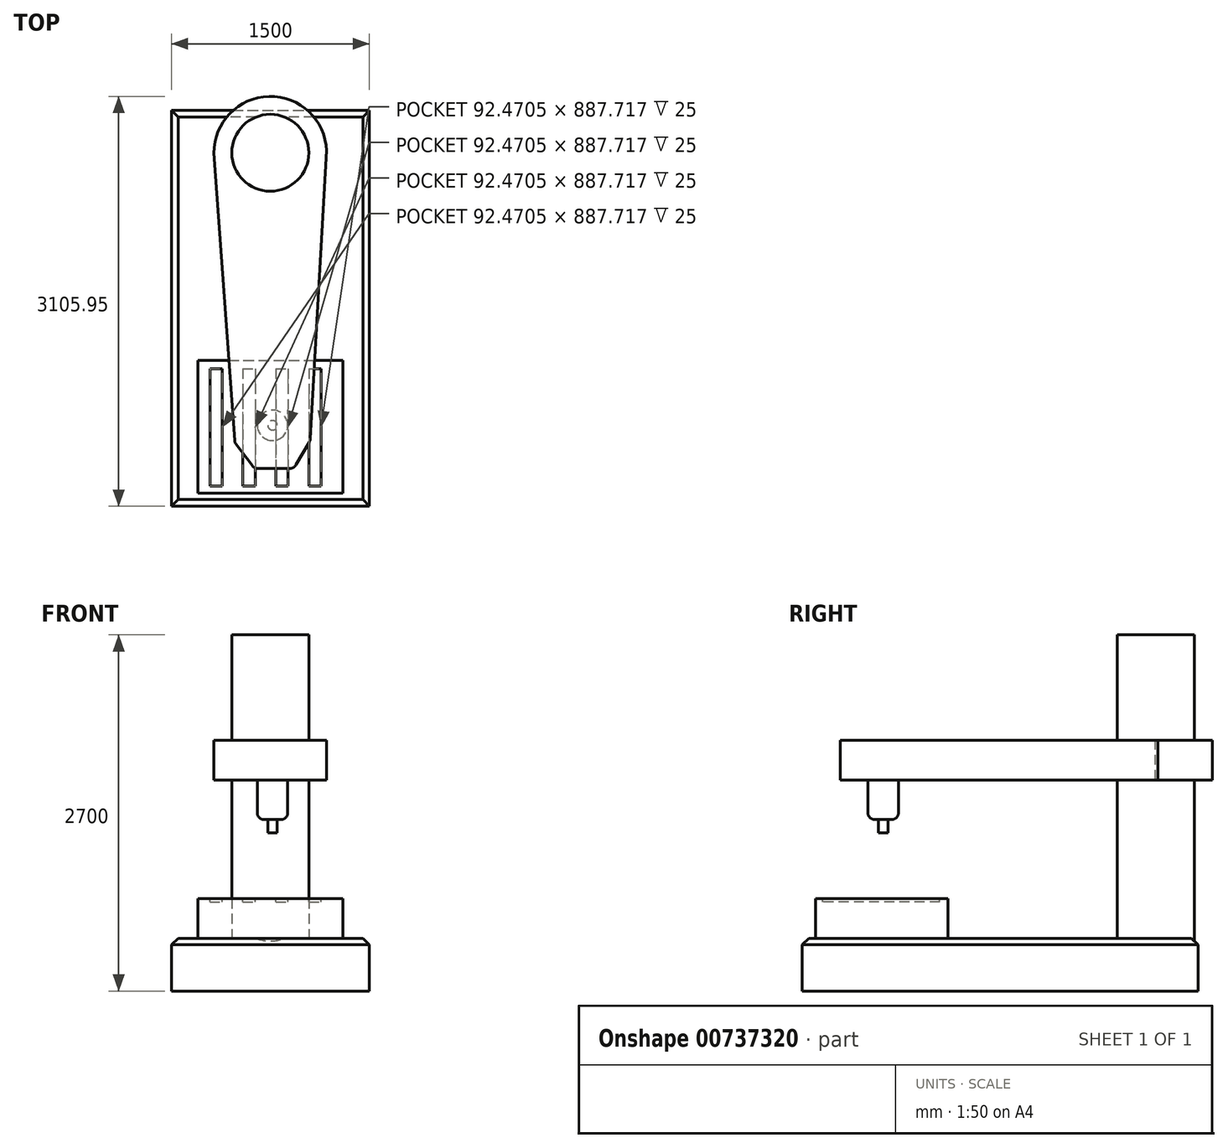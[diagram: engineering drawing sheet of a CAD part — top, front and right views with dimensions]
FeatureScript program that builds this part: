
annotation { "Feature Type Name" : "Feature", "Feature Type Description" : "" }
export const myFeature = defineFeature(function(context is Context, id is Id, definition is map)
    precondition{}
    {
        {
            var Q0;
            Q0=qCreatedBy(makeId("Top.planeOp"),FACE);
            var sketch = newSketch(context, id + "F0", { "sketchPlane" : qUnion([Q0])});
            skLineSegment(sketch, "E0.bottom", {"start": v(-749.39, 2386.8) * mm, "end": v(750.61, 2386.8) * mm});
            skLineSegment(sketch, "E0.top", {"start": v(-749.39, -613.2) * mm, "end": v(750.61, -613.2) * mm});
            skLineSegment(sketch, "E0.left", {"start": v(-749.39, 2386.8) * mm, "end": v(-749.39, -613.2) * mm});
            skLineSegment(sketch, "E0.right", {"start": v(750.61, 2386.8) * mm, "end": v(750.61, -613.2) * mm});
            skSolve(sketch);
        }
        {
            var Q0;
            Q0 = qSketchRegion(id + "F0", true);
            extrude(context, id + "F1", {"entities" : qUnion([Q0]), "depth" : 400 * mm, "offsetDistance" : 25 * mm});
        }
        {
            var Q0;
            Q0=makeQuery(id+"F1.opExtrude","CAP_FACE",FACE,{"disambiguationData":[OSD([sQuery(id+"F0.wireOp",EDGE,"E0.bottom"),sQuery(id+"F0.wireOp",EDGE,"E0.top"),sQuery(id+"F0.wireOp",EDGE,"E0.left"),sQuery(id+"F0.wireOp",EDGE,"E0.right")])],"isStart":false});
            var sketch = newSketch(context, id + "F2", { "sketchPlane" : qUnion([Q0])});
            skCircle(sketch, "E1", {"center": v(0, 2065.92) * mm, "radius": 292.28 * mm});
            skSolve(sketch);
        }
        {
            var Q0;
            Q0 = qSketchRegion(id + "F2", true);
            extrude(context, id + "F3", {"entities" : qUnion([Q0]), "operationType" : NewBodyOperationType.ADD, "depth" : 1500 * mm, "offsetDistance" : 25 * mm});
        }
        {
            var Q0;
            Q0=makeQuery(id+"F2.imprint","IMPRINT",FACE,{"disambiguationData":[TD([[makeQuery(id+"F2.imprint","IMPRINT",EDGE,{"derivedFrom":sQuery(id+"F2.wireOp",EDGE,"E1")}),-1.0]])]});
            var sketch = newSketch(context, id + "F4", { "sketchPlane" : qUnion([Q0])});
            skLineSegment(sketch, "E2.bottom", {"start": v(-549.39, 491.66) * mm, "end": v(550.61, 491.66) * mm});
            skLineSegment(sketch, "E2.top", {"start": v(-549.39, -513.2) * mm, "end": v(550.61, -513.2) * mm});
            skLineSegment(sketch, "E2.left", {"start": v(-549.39, 491.66) * mm, "end": v(-549.39, -513.2) * mm});
            skLineSegment(sketch, "E2.right", {"start": v(550.61, 491.66) * mm, "end": v(550.61, -513.2) * mm});
            skSolve(sketch);
        }
        {
            var Q0;
            Q0 = qSketchRegion(id + "F4", true);
            extrude(context, id + "F5", {"entities" : qUnion([Q0]), "depth" : 300 * mm, "offsetDistance" : 25 * mm});
        }
        {
            var Q0;
            Q0=makeQuery(id+"F5.opExtrude","CAP_FACE",FACE,{"disambiguationData":[OSD([sQuery(id+"F4.wireOp",EDGE,"E2.bottom"),sQuery(id+"F4.wireOp",EDGE,"E2.top"),sQuery(id+"F4.wireOp",EDGE,"E2.left"),sQuery(id+"F4.wireOp",EDGE,"E2.right")])],"isStart":false});
            var sketch = newSketch(context, id + "F6", { "sketchPlane" : qUnion([Q0])});
            skLineSegment(sketch, "E3.bottom", {"start": v(-457.37, 428.31) * mm, "end": v(-364.9, 428.31) * mm});
            skLineSegment(sketch, "E3.top", {"start": v(-457.37, -459.4) * mm, "end": v(-364.9, -459.4) * mm});
            skLineSegment(sketch, "E3.left", {"start": v(-457.37, 428.31) * mm, "end": v(-457.37, -459.4) * mm});
            skLineSegment(sketch, "E3.right", {"start": v(-364.9, 428.31) * mm, "end": v(-364.9, -459.4) * mm});
            skLineSegment(sketch, "E4.1.0.0", {"start": v(-207.37, 428.31) * mm, "end": v(-207.37, -459.4) * mm});
            skLineSegment(sketch, "E4.1.0.1", {"start": v(-114.9, 428.31) * mm, "end": v(-114.9, -459.4) * mm});
            skLineSegment(sketch, "E4.1.0.2", {"start": v(-207.37, -459.4) * mm, "end": v(-114.9, -459.4) * mm});
            skLineSegment(sketch, "E4.1.0.3", {"start": v(-207.37, 428.31) * mm, "end": v(-114.9, 428.31) * mm});
            skLineSegment(sketch, "E4.2.0.0", {"start": v(42.63, 428.31) * mm, "end": v(42.63, -459.4) * mm});
            skLineSegment(sketch, "E4.2.0.1", {"start": v(135.1, 428.31) * mm, "end": v(135.1, -459.4) * mm});
            skLineSegment(sketch, "E4.2.0.2", {"start": v(42.63, -459.4) * mm, "end": v(135.1, -459.4) * mm});
            skLineSegment(sketch, "E4.2.0.3", {"start": v(42.63, 428.31) * mm, "end": v(135.1, 428.31) * mm});
            skLineSegment(sketch, "E4.3.0.0", {"start": v(292.63, 428.31) * mm, "end": v(292.63, -459.4) * mm});
            skLineSegment(sketch, "E4.3.0.1", {"start": v(385.1, 428.31) * mm, "end": v(385.1, -459.4) * mm});
            skLineSegment(sketch, "E4.3.0.2", {"start": v(292.63, -459.4) * mm, "end": v(385.1, -459.4) * mm});
            skLineSegment(sketch, "E4.3.0.3", {"start": v(292.63, 428.31) * mm, "end": v(385.1, 428.31) * mm});
            skLineSegment(sketch, "E4.direction1", {"start": v(-457.37, -459.4) * mm, "end": v(-207.37, -459.4) * mm, "construction": true});
            skSolve(sketch);
        }
        {
            var Q0;
            Q0 = qSketchRegion(id + "F6", true);
            extrude(context, id + "F7", {"entities" : qUnion([Q0]), "operationType" : NewBodyOperationType.REMOVE, "oppositeDirection" : true, "depth" : 25 * mm, "offsetDistance" : 25 * mm});
        }
        {
            var Q0;
            Q0=makeQuery(id+"F3.opExtrude","CAP_FACE",FACE,{"disambiguationData":[OSD([sQuery(id+"F2.wireOp",EDGE,"E1")])],"isStart":false});
            var sketch = newSketch(context, id + "F8", { "sketchPlane" : qUnion([Q0])});
            skArc(sketch, "E5", {"start": v(-426.83, 2063.09) * mm, "mid": v(-9.46, 2492.65) * mm, "end": v(426.53, 2082.01) * mm});
            skLineSegment(sketch, "E6", {"start": v(-426.83, 2063.09) * mm, "end": v(-269.52, -131.28) * mm});
            skLineSegment(sketch, "E7", {"start": v(-269.52, -131.28) * mm, "end": v(-120.96, -326.76) * mm});
            skLineSegment(sketch, "E8", {"start": v(-120.96, -326.76) * mm, "end": v(179.04, -326.76) * mm});
            skLineSegment(sketch, "E9", {"start": v(179.04, -326.76) * mm, "end": v(302.42, -114.48) * mm});
            skLineSegment(sketch, "E10", {"start": v(302.42, -114.48) * mm, "end": v(426.53, 2082.01) * mm});
            skSolve(sketch);
        }
        {
            var Q0;
            Q0 = qSketchRegion(id + "F8", true);
            extrude(context, id + "F9", {"entities" : qUnion([Q0]), "operationType" : NewBodyOperationType.ADD, "oppositeDirection" : true, "depth" : 300 * mm, "offsetDistance" : 25 * mm});
        }
        {
            var Q0;
            Q0=makeQuery(id+"F9.opExtrude","CAP_FACE",FACE,{"disambiguationData":[OSD([sQuery(id+"F8.wireOp",EDGE,"E5"),sQuery(id+"F8.wireOp",EDGE,"E6"),sQuery(id+"F8.wireOp",EDGE,"E7"),sQuery(id+"F8.wireOp",EDGE,"E8"),sQuery(id+"F8.wireOp",EDGE,"E9"),sQuery(id+"F8.wireOp",EDGE,"E10")])],"isStart":false});
            var sketch = newSketch(context, id + "F10", { "sketchPlane" : qUnion([Q0])});
            skCircle(sketch, "E11", {"center": v(16.48, 0) * mm, "radius": 115.34 * mm});
            skSolve(sketch);
        }
        {
            var Q0;
            Q0 = qSketchRegion(id + "F10", true);
            extrude(context, id + "F11", {"entities" : qUnion([Q0]), "operationType" : NewBodyOperationType.ADD, "depth" : 300 * mm, "offsetDistance" : 25 * mm});
        }
        {
            var Q0;
            Q0=makeQuery(id+"F11.opExtrude","CAP_EDGE",EDGE,{"disambiguationData":[OSD([sQuery(id+"F10.wireOp",EDGE,"E11")])],"isStart":false});
            fillet(context, id + "F12", {"entities" : qUnion([Q0]), "radius" : 50 * mm, "tangentPropagation" : true, "allowEdgeOverflow" : false});
        }
        {
            var Q0;
            Q0=makeQuery(id+"F11.opExtrude","CAP_FACE",FACE,{"disambiguationData":[OSD([sQuery(id+"F10.wireOp",EDGE,"E11")])],"isStart":false});
            var sketch = newSketch(context, id + "F13", { "sketchPlane" : qUnion([Q0])});
            skCircle(sketch, "E12", {"center": v(16.48, 0) * mm, "radius": 36.46 * mm});
            skSolve(sketch);
        }
        {
            var Q0;
            Q0 = qSketchRegion(id + "F13", true);
            extrude(context, id + "F14", {"entities" : qUnion([Q0]), "operationType" : NewBodyOperationType.ADD, "depth" : 100 * mm, "offsetDistance" : 25 * mm});
        }
        {
            var Q0;
            Q0=makeQuery(id+"F1.opExtrude","CAP_EDGE",EDGE,{"disambiguationData":[OSD([sQuery(id+"F0.wireOp",EDGE,"E0.right")])],"isStart":false});
            var Q1;
            Q1=makeQuery(id+"F1.opExtrude","CAP_EDGE",EDGE,{"disambiguationData":[OSD([sQuery(id+"F0.wireOp",EDGE,"E0.top")])],"isStart":false});
            var Q2;
            Q2=makeQuery(id+"F1.opExtrude","CAP_EDGE",EDGE,{"disambiguationData":[OSD([sQuery(id+"F0.wireOp",EDGE,"E0.left")])],"isStart":false});
            var Q3;
            Q3=makeQuery(id+"F1.opExtrude","CAP_EDGE",EDGE,{"disambiguationData":[OSD([sQuery(id+"F0.wireOp",EDGE,"E0.bottom")])],"isStart":false});
            chamfer(context, id + "F15", {"entities" : qUnion([Q0, Q1, Q2, Q3]), "width" : 50 * mm, "tangentPropagation" : true});
        }
        {
            var Q0;
            Q0=makeQuery(id+"F9.opExtrude","SWEPT_EDGE",EDGE,{"disambiguationData":[OSD([sQuery(id+"F8.wireOp",EDGE,"E9"),sQuery(id+"F8.wireOp",EDGE,"E10")])]});
            var Q1;
            Q1=makeQuery(id+"F9.opExtrude","SWEPT_EDGE",EDGE,{"disambiguationData":[OSD([sQuery(id+"F8.wireOp",EDGE,"E8"),sQuery(id+"F8.wireOp",EDGE,"E9")])]});
            var Q2;
            Q2=makeQuery(id+"F9.opExtrude","SWEPT_EDGE",EDGE,{"disambiguationData":[OSD([sQuery(id+"F8.wireOp",EDGE,"E7"),sQuery(id+"F8.wireOp",EDGE,"E8")])]});
            var Q3;
            Q3=makeQuery(id+"F9.opExtrude","SWEPT_EDGE",EDGE,{"disambiguationData":[OSD([sQuery(id+"F8.wireOp",EDGE,"E6"),sQuery(id+"F8.wireOp",EDGE,"E7")])]});
            fillet(context, id + "F16", {"entities" : qUnion([Q0, Q1, Q2, Q3]), "radius" : 55 * mm, "tangentPropagation" : true, "allowEdgeOverflow" : false});
        }
        {
            var Q0;
            Q0=makeQuery(id+"F9.boolean.opBoolean","MERGE",FACE,{"derivedFrom":[makeQuery(id+"F3.opExtrude","CAP_FACE",FACE,{"disambiguationData":[OSD([sQuery(id+"F2.wireOp",EDGE,"E1")])],"isStart":false}),makeQuery(id+"F9.opExtrude","CAP_FACE",FACE,{"disambiguationData":[OSD([sQuery(id+"F8.wireOp",EDGE,"E5"),sQuery(id+"F8.wireOp",EDGE,"E6"),sQuery(id+"F8.wireOp",EDGE,"E7"),sQuery(id+"F8.wireOp",EDGE,"E8"),sQuery(id+"F8.wireOp",EDGE,"E9"),sQuery(id+"F8.wireOp",EDGE,"E10")])],"isStart":true})]});
            var sketch = newSketch(context, id + "F17", { "sketchPlane" : qUnion([Q0])});
            skCircle(sketch, "E13", {"center": v(0, 2065.92) * mm, "radius": 291.6 * mm});
            skSolve(sketch);
        }
        {
            var Q0;
            Q0 = qSketchRegion(id + "F17", true);
            extrude(context, id + "F18", {"entities" : qUnion([Q0]), "operationType" : NewBodyOperationType.ADD, "depth" : 800 * mm, "offsetDistance" : 25 * mm});
        }
    });
